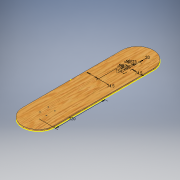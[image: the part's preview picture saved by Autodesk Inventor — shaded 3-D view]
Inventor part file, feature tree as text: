
AUTODESK INVENTOR PART (.ipt)
format: ipt  version: 2019 (Build 230136000, 136)  size: 154,112 bytes
history: native  units: mm
features: sketch x3, hole x2, other x1, extrude x1
ambient origin geometry x8: Origin, YZ Plane, XZ Plane, XY Plane, X Axis, Y Axis, Z Axis, Center Point
bodies: Body1 (feature_tree)
feature tree (7):
  other  "ソリッド1"
  sketch  "スケッチ1"
  extrude  "押し出し1"  Depth=270.0mm
  sketch  "スケッチ4"
  hole  "穴2"  [1 undecoded]
  hole  "穴3"  [1 undecoded]
  sketch  "スケッチ2"
note: 2 required parameter values undecoded (feature->parameter linkage not recoverable at this tier; creation-order binding heuristic only, values carry confidence <= 0.55)
